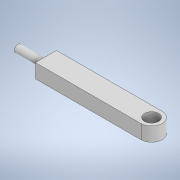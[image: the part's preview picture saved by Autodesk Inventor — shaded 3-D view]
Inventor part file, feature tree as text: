
AUTODESK INVENTOR PART (.ipt)
format: ipt  version: 2021 (Build 250183000, 183)  size: 108,032 bytes
history: native  units: in
note: dims shown in document units (in); Inventor stores cm internally (conversion verified against a paired STEP export)
features: sketch x4, extrude x2, hole x1
ambient origin geometry x8: Origin, YZ Plane, XZ Plane, XY Plane, X Axis, Y Axis, Z Axis, Center Point
bodies: Solid1 (feature_tree)
feature tree (7):
  sketch  "Sketch1"  dims[d0=0.2953in d1=2.9528in]
  extrude  "Extrusion1"  Depth=0.2953in
  hole  "Hole1"  [1 undecoded]
  extrude  "Extrusion2"  Depth=0.1969in
  sketch  "Sketch2"  dims[d2=0.5906in d5=0.3937in d6=0.0in]
  sketch  "Sketch3"  dims[d7=0.3937in d8=0.2362in d9=0.1575in d10=0.0787in d11=90.0deg d12=0.315in d13=0.8108in d14=0.1969in]
  sketch  "Sketch4"  dims[d15=0.7874in d16=0.0in]
note: 1 required parameter value undecoded (feature->parameter linkage not recoverable at this tier; creation-order binding heuristic only, values carry confidence <= 0.55)
